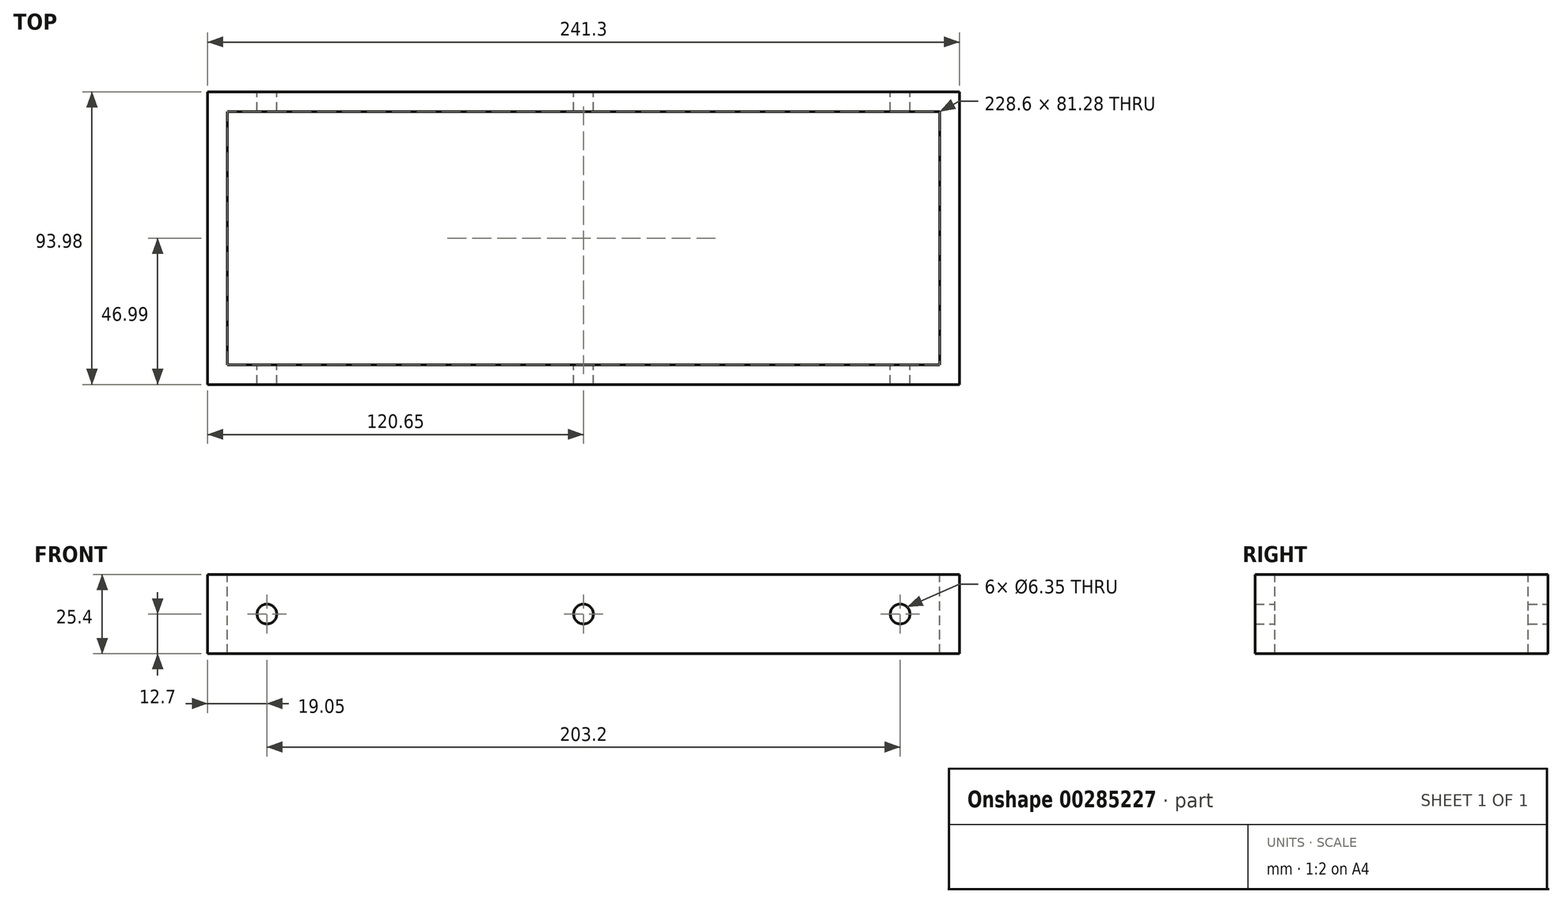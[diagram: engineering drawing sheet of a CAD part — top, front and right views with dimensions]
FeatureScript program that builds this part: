
annotation { "Feature Type Name" : "Feature", "Feature Type Description" : "" }
export const myFeature = defineFeature(function(context is Context, id is Id, definition is map)
    precondition{}
    {
        {
            var Q0;
            Q0=qCreatedBy(makeId("Front.planeOp"),FACE);
            var sketch = newSketch(context, id + "F0", { "sketchPlane" : qUnion([Q0])});
            skLineSegment(sketch, "E0.bottom", {"start": v(0, 0) * mm, "end": v(241.3, 0) * mm});
            skLineSegment(sketch, "E0.top", {"start": v(0, 25.4) * mm, "end": v(241.3, 25.4) * mm});
            skLineSegment(sketch, "E0.left", {"start": v(0, 0) * mm, "end": v(0, 25.4) * mm});
            skLineSegment(sketch, "E0.right", {"start": v(241.3, 0) * mm, "end": v(241.3, 25.4) * mm});
            skLineSegment(sketch, "E1", {"start": v(120.65, 25.4) * mm, "end": v(120.65, 12.7) * mm});
            skLineSegment(sketch, "E2", {"start": v(0, 12.7) * mm, "end": v(19.05, 12.7) * mm});
            skLineSegment(sketch, "E3", {"start": v(241.3, 12.7) * mm, "end": v(222.25, 12.7) * mm});
            skCircle(sketch, "E4", {"center": v(120.65, 12.7) * mm, "radius": 3.18 * mm});
            skCircle(sketch, "E5", {"center": v(222.25, 12.7) * mm, "radius": 3.18 * mm});
            skCircle(sketch, "E6", {"center": v(19.05, 12.7) * mm, "radius": 3.18 * mm});
            skSolve(sketch);
        }
        {
            var Q0;
            {var subQ1=sQuery(id+"F0.wireOp",EDGE,"E0.bottom");Q0=makeQuery(id+"F0.imprint","IMPRINT",FACE,{"disambiguationData":[TD([[makeQuery(id+"F0.imprint","IMPRINT",EDGE,{"derivedFrom":subQ1}),1.0]])]});}
            extrude(context, id + "F1", {"entities" : qUnion([Q0]), "depth" : 6.35 * mm});
        }
        {
            var Q0;
            Q0=makeQuery(id+"F1.opExtrude","CAP_FACE",FACE,{"disambiguationData":[OSD([sQuery(id+"F0.wireOp",EDGE,"E0.bottom"),sQuery(id+"F0.wireOp",EDGE,"E0.top"),sQuery(id+"F0.wireOp",EDGE,"E0.left"),sQuery(id+"F0.wireOp",EDGE,"E0.right"),sQuery(id+"F0.wireOp",EDGE,"E4"),sQuery(id+"F0.wireOp",EDGE,"E5"),sQuery(id+"F0.wireOp",EDGE,"E6")])],"isStart":false});
            var sketch = newSketch(context, id + "F2", { "sketchPlane" : qUnion([Q0])});
            skLineSegment(sketch, "E7.bottom", {"start": v(0, 0) * mm, "end": v(6.35, 0) * mm});
            skLineSegment(sketch, "E7.top", {"start": v(0, 25.4) * mm, "end": v(6.35, 25.4) * mm});
            skLineSegment(sketch, "E7.left", {"start": v(0, 0) * mm, "end": v(0, 25.4) * mm});
            skLineSegment(sketch, "E7.right", {"start": v(6.35, 0) * mm, "end": v(6.35, 25.4) * mm});
            skLineSegment(sketch, "E8.bottom", {"start": v(241.3, 0) * mm, "end": v(234.95, 0) * mm});
            skLineSegment(sketch, "E8.top", {"start": v(241.3, 25.4) * mm, "end": v(234.95, 25.4) * mm});
            skLineSegment(sketch, "E8.left", {"start": v(241.3, 0) * mm, "end": v(241.3, 25.4) * mm});
            skLineSegment(sketch, "E8.right", {"start": v(234.95, 0) * mm, "end": v(234.95, 25.4) * mm});
            skSolve(sketch);
        }
        {
            var Q0;
            Q0=makeQuery(id+"F2.imprint","IMPRINT",FACE,{"disambiguationData":[TD([[makeQuery(id+"F2.imprint","IMPRINT",EDGE,{"derivedFrom":sQuery(id+"F2.wireOp",EDGE,"E7.bottom")}),1.0]])]});
            var Q1;
            Q1=makeQuery(id+"F2.imprint","IMPRINT",FACE,{"disambiguationData":[TD([[makeQuery(id+"F2.imprint","IMPRINT",EDGE,{"derivedFrom":sQuery(id+"F2.wireOp",EDGE,"E8.bottom")}),1.0]])]});
            extrude(context, id + "F3", {"entities" : qUnion([Q0, Q1]), "operationType" : NewBodyOperationType.ADD, "depth" : 81.28 * mm});
        }
        {
            var Q0;
            Q0=makeQuery(id+"F3.opExtrude","CAP_FACE",FACE,{"disambiguationData":[OSD([sQuery(id+"F2.wireOp",EDGE,"E7.bottom"),sQuery(id+"F2.wireOp",EDGE,"E7.top"),sQuery(id+"F2.wireOp",EDGE,"E7.left"),sQuery(id+"F2.wireOp",EDGE,"E7.right")])],"isStart":false});
            var sketch = newSketch(context, id + "F4", { "sketchPlane" : qUnion([Q0])});
            skLineSegment(sketch, "E9.bottom", {"start": v(0, 0) * mm, "end": v(241.3, 0) * mm});
            skLineSegment(sketch, "E9.top", {"start": v(0, 25.4) * mm, "end": v(241.3, 25.4) * mm});
            skLineSegment(sketch, "E9.left", {"start": v(0, 0) * mm, "end": v(0, 25.4) * mm});
            skLineSegment(sketch, "E9.right", {"start": v(241.3, 0) * mm, "end": v(241.3, 25.4) * mm});
            skSolve(sketch);
        }
        {
            var Q0;
            {var subQ2=sQuery(id+"F4.wireOp",EDGE,"E9.right");Q0=makeQuery(id+"F4.imprint","IMPRINT",FACE,{"disambiguationData":[TD([[makeQuery(id+"F4.imprint","IMPRINT",EDGE,{"derivedFrom":subQ2}),1.0]])]});}
            var Q1;
            {var subQ0=sQuery(id+"F4.wireOp",EDGE,"E9.left");Q1=makeQuery(id+"F4.imprint","IMPRINT",FACE,{"disambiguationData":[TD([[makeQuery(id+"F4.imprint","IMPRINT",EDGE,{"derivedFrom":subQ0}),-1.0]])]});}
            extrude(context, id + "F5", {"entities" : qUnion([Q0, Q1]), "operationType" : NewBodyOperationType.ADD, "depth" : 6.35 * mm});
        }
        {
            var Q0;
            Q0=makeQuery(id+"F1.opExtrude","CAP_FACE",FACE,{"disambiguationData":[OSD([sQuery(id+"F0.wireOp",EDGE,"E0.bottom"),sQuery(id+"F0.wireOp",EDGE,"E0.top"),sQuery(id+"F0.wireOp",EDGE,"E0.left"),sQuery(id+"F0.wireOp",EDGE,"E0.right"),sQuery(id+"F0.wireOp",EDGE,"E4"),sQuery(id+"F0.wireOp",EDGE,"E5"),sQuery(id+"F0.wireOp",EDGE,"E6")])],"isStart":false});
            var sketch = newSketch(context, id + "F6", { "sketchPlane" : qUnion([Q0])});
            skCircle(sketch, "E10", {"center": v(19.05, 12.7) * mm, "radius": 3.18 * mm});
            skCircle(sketch, "E11", {"center": v(120.65, 12.7) * mm, "radius": 3.18 * mm});
            skCircle(sketch, "E12", {"center": v(222.25, 12.7) * mm, "radius": 3.18 * mm});
            skSolve(sketch);
        }
        {
            var Q0;
            Q0=makeQuery(id+"F6.imprint","IMPRINT",FACE,{"disambiguationData":[TD([[makeQuery(id+"F6.imprint","IMPRINT",EDGE,{"derivedFrom":sQuery(id+"F6.wireOp",EDGE,"E12")}),1.0]])]});
            var Q1;
            Q1=makeQuery(id+"F6.imprint","IMPRINT",FACE,{"disambiguationData":[TD([[makeQuery(id+"F6.imprint","IMPRINT",EDGE,{"derivedFrom":sQuery(id+"F6.wireOp",EDGE,"E11")}),1.0]])]});
            var Q2;
            Q2=makeQuery(id+"F6.imprint","IMPRINT",FACE,{"disambiguationData":[TD([[makeQuery(id+"F6.imprint","IMPRINT",EDGE,{"derivedFrom":sQuery(id+"F6.wireOp",EDGE,"E10")}),1.0]])]});
            extrude(context, id + "F7", {"entities" : qUnion([Q0, Q1, Q2]), "operationType" : NewBodyOperationType.REMOVE, "depth" : 508 * mm});
        }
    });
